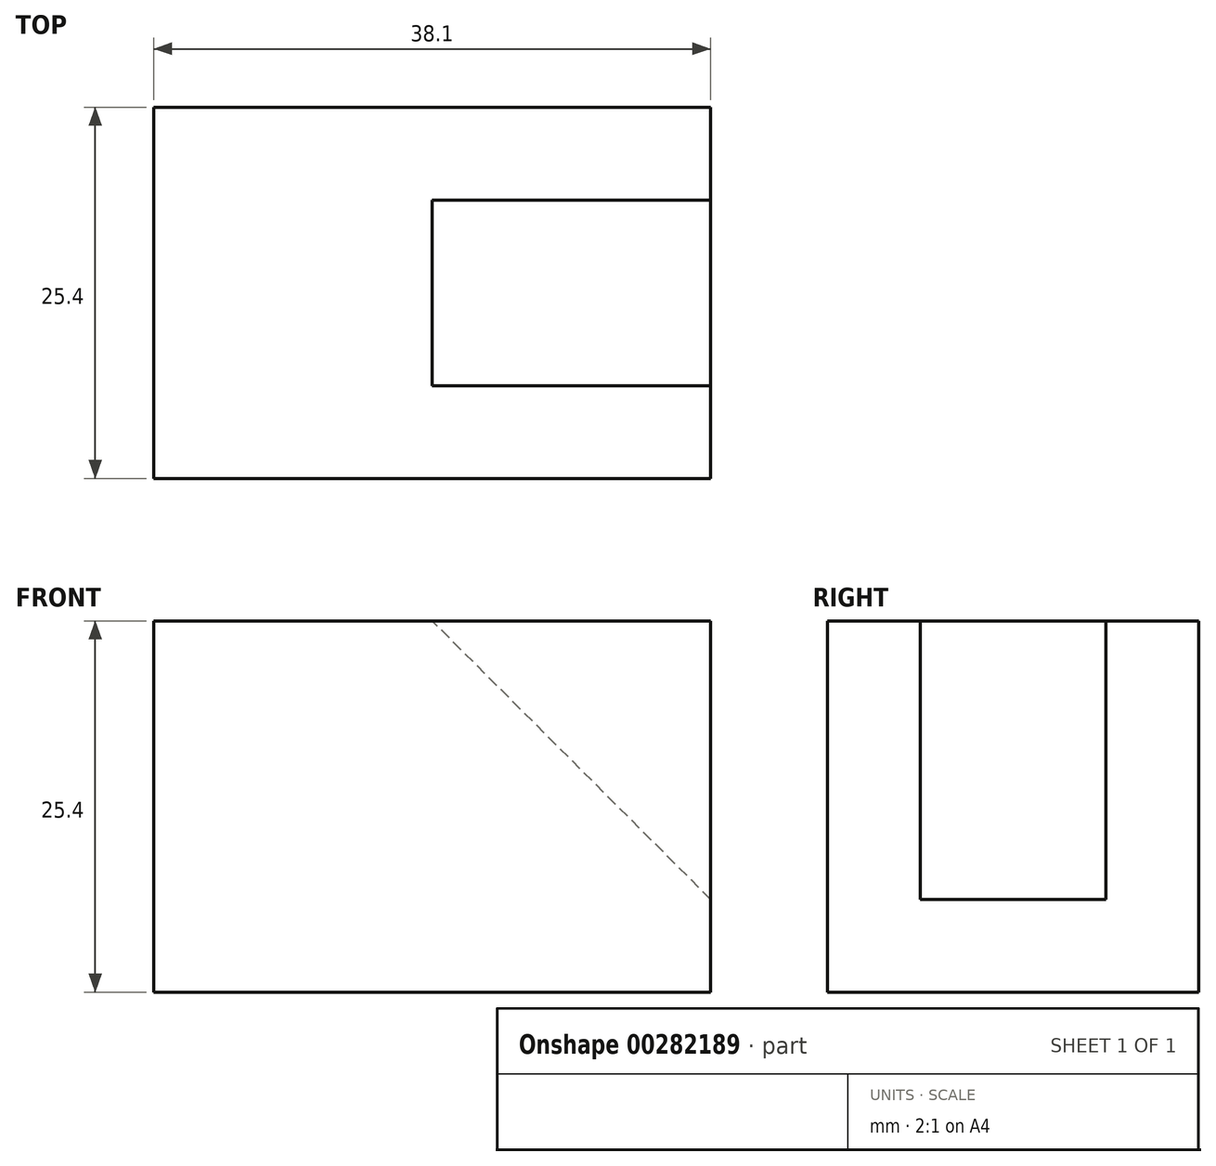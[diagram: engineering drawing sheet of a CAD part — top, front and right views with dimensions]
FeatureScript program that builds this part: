
annotation { "Feature Type Name" : "Feature", "Feature Type Description" : "" }
export const myFeature = defineFeature(function(context is Context, id is Id, definition is map)
    precondition{}
    {
        {
            var Q0;
            Q0=qCreatedBy(makeId("Top.planeOp"),FACE);
            var sketch = newSketch(context, id + "F0", { "sketchPlane" : qUnion([Q0])});
            skLineSegment(sketch, "E0.bottom", {"start": v(0, 12.7) * mm, "end": v(38.1, 12.7) * mm});
            skLineSegment(sketch, "E0.top", {"start": v(0, -12.7) * mm, "end": v(38.1, -12.7) * mm});
            skLineSegment(sketch, "E0.left", {"start": v(0, 12.7) * mm, "end": v(0, -12.7) * mm});
            skLineSegment(sketch, "E0.right", {"start": v(38.1, 12.7) * mm, "end": v(38.1, -12.7) * mm});
            skSolve(sketch);
        }
        {
            var Q0;
            Q0 = qSketchRegion(id + "F0", true);
            extrude(context, id + "F1", {"entities" : qUnion([Q0]), "depth" : 25.4 * mm});
        }
        {
            var Q0;
            Q0=qCreatedBy(makeId("Front.planeOp"),FACE);
            var sketch = newSketch(context, id + "F2", { "sketchPlane" : qUnion([Q0])});
            skLineSegment(sketch, "E1", {"start": v(19.05, 25.4) * mm, "end": v(38.1, 25.4) * mm});
            skLineSegment(sketch, "E2", {"start": v(38.1, 25.4) * mm, "end": v(38.1, 6.35) * mm});
            skLineSegment(sketch, "E3", {"start": v(38.1, 6.35) * mm, "end": v(19.05, 25.4) * mm});
            skSolve(sketch);
        }
        {
            var Q0;
            Q0 = qSketchRegion(id + "F2", true);
            extrude(context, id + "F3", {"entities" : qUnion([Q0]), "operationType" : NewBodyOperationType.REMOVE, "oppositeDirection" : true, "depth" : 6.35 * mm, "hasSecondDirection" : true, "secondDirectionOppositeDirection" : false, "secondDirectionDepth" : 6.35 * mm});
        }
    });
